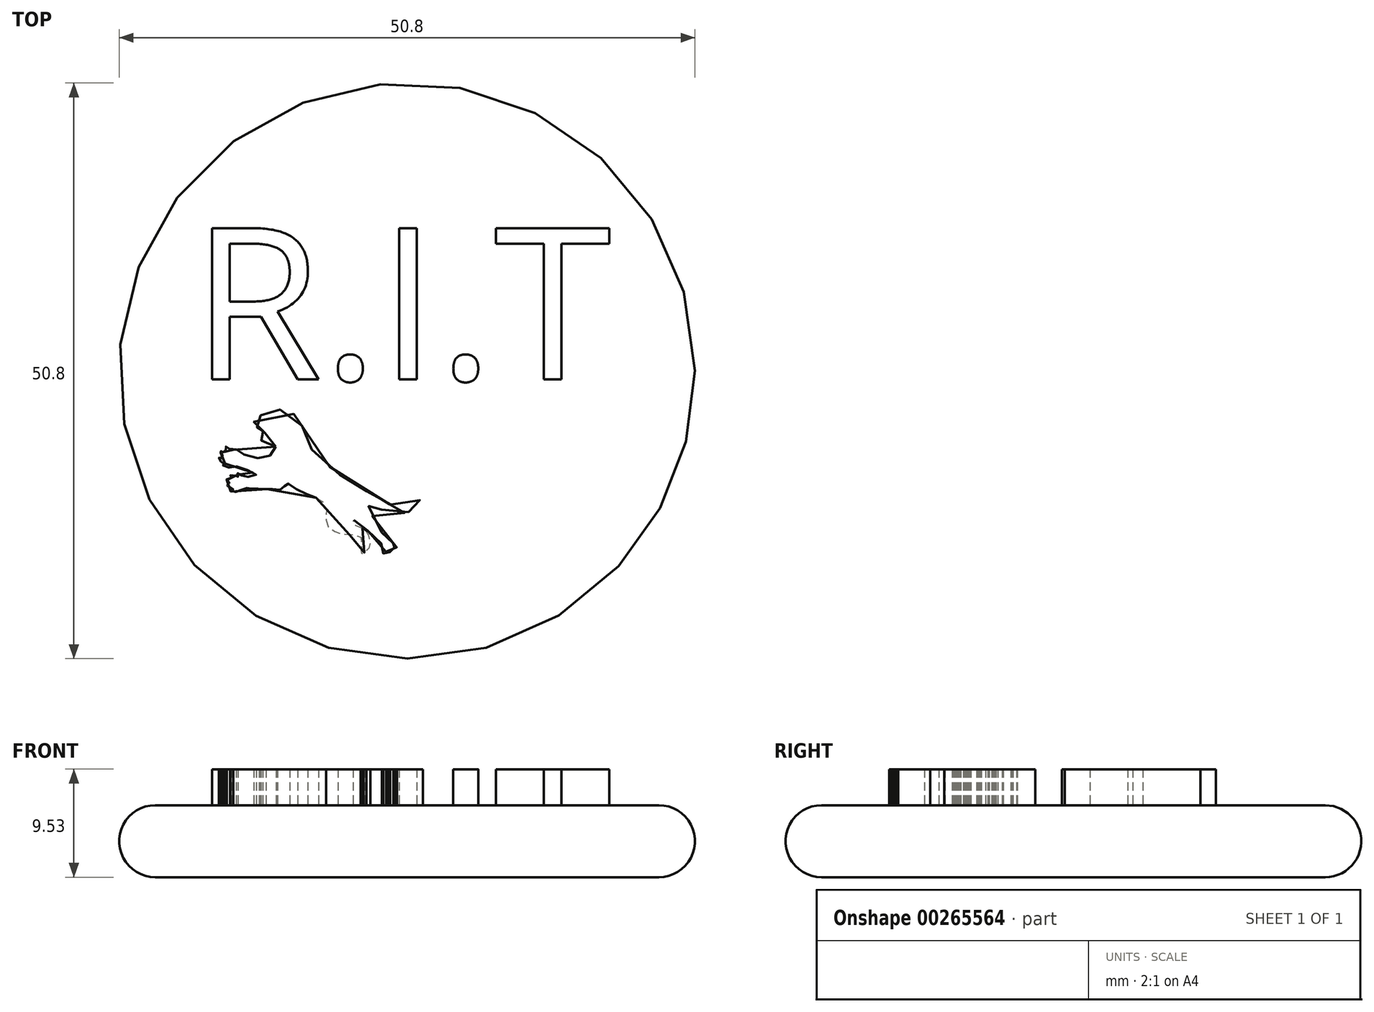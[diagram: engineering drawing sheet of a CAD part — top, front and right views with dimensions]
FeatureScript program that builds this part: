
annotation { "Feature Type Name" : "Feature", "Feature Type Description" : "" }
export const myFeature = defineFeature(function(context is Context, id is Id, definition is map)
    precondition{}
    {
        {
            var Q0;
            Q0=qCreatedBy(makeId("Top.planeOp"),FACE);
            var sketch = newSketch(context, id + "F0", { "sketchPlane" : qUnion([Q0])});
            skCircle(sketch, "E0", {"center": v(0, 0) * mm, "radius": 25.4 * mm});
            skText(sketch, "E1", { "text": "R.I.T\n", "fontName": "OpenSans-Regular.ttf"});
            skLineSegment(sketch, "E2", {"start": v(-19.05, 12.7) * mm, "end": v(19.05, -0.76) * mm});
            skPoint(sketch, "E3", {"position": v(0, 5.97) * mm});
            const initialGuessF0  = {"E1": [-0.01905, -0.00076, 1, 0, 0.01346]};
            skSetInitialGuess(sketch, initialGuessF0);
            skSolve(sketch);
        }
        {
            var Q0;
            Q0=makeQuery(id+"F0.imprint","IMPRINT",FACE,{"disambiguationData":[TD([[makeQuery(id+"F0.imprint","IMPRINT",EDGE,{"derivedFrom":sQuery(id+"F0.wireOp",EDGE,"E0")}),1.0]])]});
            var Q1;
            Q1=makeQuery(id+"F0.imprint","IMPRINT",FACE,{"disambiguationData":[TD([[makeQuery(id+"F0.imprint","IMPRINT",EDGE,{"derivedFrom":sQuery(id+"F0.wireOp",EDGE,"E1.sketch_text.stroke-11")}),1.0]])]});
            var Q2;
            {var subQ0=sQuery(id+"F0.wireOp",EDGE,"E1.sketch_text.stroke-15");Q2=makeQuery(id+"F0.imprint","IMPRINT",FACE,{"disambiguationData":[TD([[makeQuery(id+"F0.imprint","IMPRINT",EDGE,{"derivedFrom":subQ0}),1.0]])]});}
            extrude(context, id + "F1", {"entities" : qUnion([Q0, Q1, Q2]), "depth" : 6.35 * mm});
        }
        {
            var Q0;
            Q0=makeQuery(id+"F0.imprint","IMPRINT",FACE,{"disambiguationData":[TD([[makeQuery(id+"F0.imprint","IMPRINT",EDGE,{"derivedFrom":sQuery(id+"F0.wireOp",EDGE,"E1.sketch_text.stroke-18")}),-1.0]])]});
            var Q1;
            Q1=makeQuery(id+"F0.imprint","IMPRINT",FACE,{"disambiguationData":[TD([[makeQuery(id+"F0.imprint","IMPRINT",EDGE,{"derivedFrom":sQuery(id+"F0.wireOp",EDGE,"E1.sketch_text.stroke-30")}),-1.0]])]});
            var Q2;
            {var subQ0=sQuery(id+"F0.wireOp",EDGE,"E1.sketch_text.stroke-29");Q2=makeQuery(id+"F0.imprint","IMPRINT",FACE,{"disambiguationData":[TD([[makeQuery(id+"F0.imprint","IMPRINT",EDGE,{"derivedFrom":subQ0}),-1.0]])]});}
            var Q3;
            {var subQ0=sQuery(id+"F0.wireOp",EDGE,"E1.sketch_text.stroke-27");Q3=makeQuery(id+"F0.imprint","IMPRINT",FACE,{"disambiguationData":[TD([[makeQuery(id+"F0.imprint","IMPRINT",EDGE,{"derivedFrom":subQ0}),-1.0]])]});}
            var Q4;
            Q4=makeQuery(id+"F0.imprint","IMPRINT",FACE,{"disambiguationData":[TD([[makeQuery(id+"F0.imprint","IMPRINT",EDGE,{"derivedFrom":sQuery(id+"F0.wireOp",EDGE,"E1.sketch_text.stroke-0")}),-1.0]])]});
            var Q5;
            {var subQ7=sQuery(id+"F0.wireOp",EDGE,"E1.sketch_text.stroke-3");Q5=makeQuery(id+"F0.imprint","IMPRINT",FACE,{"disambiguationData":[TD([[makeQuery(id+"F0.imprint","IMPRINT",EDGE,{"derivedFrom":subQ7}),-1.0]])]});}
            var Q6;
            {var subQ0=sQuery(id+"F0.wireOp",EDGE,"E1.sketch_text.stroke-40");Q6=makeQuery(id+"F0.imprint","IMPRINT",FACE,{"disambiguationData":[TD([[makeQuery(id+"F0.imprint","IMPRINT",EDGE,{"derivedFrom":subQ0}),-1.0]])]});}
            var Q7;
            {var subQ0=sQuery(id+"F0.wireOp",EDGE,"E1.sketch_text.stroke-38");Q7=makeQuery(id+"F0.imprint","IMPRINT",FACE,{"disambiguationData":[TD([[makeQuery(id+"F0.imprint","IMPRINT",EDGE,{"derivedFrom":subQ0}),-1.0]])]});}
            extrude(context, id + "F2", {"entities" : qUnion([Q0, Q1, Q2, Q3, Q4, Q5, Q6, Q7]), "operationType" : NewBodyOperationType.ADD, "depth" : 9.52 * mm});
        }
        {
            var Q0;
            Q0=makeQuery(id+"F1.opExtrude","CAP_EDGE",EDGE,{"disambiguationData":[OSD([sQuery(id+"F0.wireOp",EDGE,"E0")])],"isStart":false});
            var Q1;
            Q1=makeQuery(id+"F1.opExtrude","CAP_EDGE",EDGE,{"disambiguationData":[OSD([sQuery(id+"F0.wireOp",EDGE,"E0")])],"isStart":true});
            fillet(context, id + "F3", {"entities" : qUnion([Q0, Q1]), "radius" : 3.17 * mm, "tangentPropagation" : true, "allowEdgeOverflow" : false});
        }
        {
            var Q0;
            Q0=makeQuery(id+"F1.opExtrude","CAP_FACE",FACE,{"disambiguationData":[OSD([sQuery(id+"F0.wireOp",EDGE,"E0"),sQuery(id+"F0.wireOp",EDGE,"E1.sketch_text.stroke-0"),sQuery(id+"F0.wireOp",EDGE,"E1.sketch_text.stroke-1"),sQuery(id+"F0.wireOp",EDGE,"E1.sketch_text.stroke-2"),sQuery(id+"F0.wireOp",EDGE,"E1.sketch_text.stroke-3"),sQuery(id+"F0.wireOp",EDGE,"E1.sketch_text.stroke-4"),sQuery(id+"F0.wireOp",EDGE,"E1.sketch_text.stroke-5"),sQuery(id+"F0.wireOp",EDGE,"E1.sketch_text.stroke-6"),sQuery(id+"F0.wireOp",EDGE,"E1.sketch_text.stroke-7"),sQuery(id+"F0.wireOp",EDGE,"E1.sketch_text.stroke-8"),sQuery(id+"F0.wireOp",EDGE,"E1.sketch_text.stroke-9"),sQuery(id+"F0.wireOp",EDGE,"E1.sketch_text.stroke-10"),sQuery(id+"F0.wireOp",EDGE,"E1.sketch_text.stroke-18"),sQuery(id+"F0.wireOp",EDGE,"E1.sketch_text.stroke-19"),sQuery(id+"F0.wireOp",EDGE,"E1.sketch_text.stroke-20"),sQuery(id+"F0.wireOp",EDGE,"E1.sketch_text.stroke-21"),sQuery(id+"F0.wireOp",EDGE,"E1.sketch_text.stroke-22"),sQuery(id+"F0.wireOp",EDGE,"E1.sketch_text.stroke-23"),sQuery(id+"F0.wireOp",EDGE,"E1.sketch_text.stroke-24"),sQuery(id+"F0.wireOp",EDGE,"E1.sketch_text.stroke-25"),sQuery(id+"F0.wireOp",EDGE,"E1.sketch_text.stroke-26"),sQuery(id+"F0.wireOp",EDGE,"E1.sketch_text.stroke-27"),sQuery(id+"F0.wireOp",EDGE,"E1.sketch_text.stroke-28"),sQuery(id+"F0.wireOp",EDGE,"E1.sketch_text.stroke-29"),sQuery(id+"F0.wireOp",EDGE,"E1.sketch_text.stroke-30"),sQuery(id+"F0.wireOp",EDGE,"E1.sketch_text.stroke-31"),sQuery(id+"F0.wireOp",EDGE,"E1.sketch_text.stroke-32"),sQuery(id+"F0.wireOp",EDGE,"E1.sketch_text.stroke-33"),sQuery(id+"F0.wireOp",EDGE,"E1.sketch_text.stroke-34"),sQuery(id+"F0.wireOp",EDGE,"E1.sketch_text.stroke-35"),sQuery(id+"F0.wireOp",EDGE,"E1.sketch_text.stroke-36"),sQuery(id+"F0.wireOp",EDGE,"E1.sketch_text.stroke-37"),sQuery(id+"F0.wireOp",EDGE,"E1.sketch_text.stroke-38"),sQuery(id+"F0.wireOp",EDGE,"E1.sketch_text.stroke-39"),sQuery(id+"F0.wireOp",EDGE,"E1.sketch_text.stroke-40"),sQuery(id+"F0.wireOp",EDGE,"E1.sketch_text.stroke-41"),sQuery(id+"F0.wireOp",EDGE,"E1.sketch_text.stroke-42"),sQuery(id+"F0.wireOp",EDGE,"E1.sketch_text.stroke-43"),sQuery(id+"F0.wireOp",EDGE,"E1.sketch_text.stroke-44"),sQuery(id+"F0.wireOp",EDGE,"E1.sketch_text.stroke-45")])],"isStart":false});
            var sketch = newSketch(context, id + "F4", { "sketchPlane" : qUnion([Q0])});
            skFitSpline(sketch, "E4", {"points": [v(-11.58, -6.67) * mm, v(-11.81, -7.02) * mm, v(-12.17, -7.55) * mm, v(-12.83, -7.73) * mm, v(-13.73, -7.57) * mm, v(-14.45, -7.34) * mm, v(-14.84, -7.04) * mm, v(-15.06, -6.93) * mm, v(-15.18, -7.06) * mm, v(-15.43, -6.95) * mm, v(-15.8, -6.87) * mm, v(-15.9, -6.83) * mm, v(-15.98, -6.83) * mm, v(-16.01, -6.75) * mm, v(-15.97, -6.67) * mm, v(-16.04, -6.7) * mm, v(-16.07, -6.81) * mm, v(-16.04, -6.96) * mm, v(-16.01, -7.01) * mm, v(-16.01, -7.13) * mm, v(-16.15, -7.1) * mm, v(-16.26, -7.13) * mm, v(-16.3, -7.2) * mm, v(-16.35, -7.16) * mm, v(-16.38, -7.07) * mm, v(-16.35, -7) * mm, v(-16.4, -7.03) * mm, v(-16.45, -7.12) * mm, v(-16.43, -7.28) * mm, v(-16.31, -7.42) * mm, v(-16.3, -7.4) * mm, v(-16.28, -7.48) * mm, v(-16.2, -7.55) * mm, v(-16.3, -7.55) * mm, v(-16.43, -7.65) * mm, v(-16.46, -7.73) * mm, v(-16.5, -7.7) * mm, v(-16.54, -7.66) * mm, v(-16.53, -7.53) * mm, v(-16.59, -7.58) * mm, v(-16.6, -7.71) * mm, v(-16.59, -7.83) * mm, v(-16.48, -7.9) * mm, v(-16.45, -8) * mm, v(-16.36, -8.07) * mm, v(-16.22, -8.14) * mm, v(-16.05, -8.14) * mm, v(-16.11, -8.2) * mm, v(-16.13, -8.35) * mm, v(-16.22, -8.32) * mm, v(-16.23, -8.22) * mm, v(-16.25, -8.3) * mm, v(-16.2, -8.45) * mm, v(-16, -8.52) * mm, v(-15.7, -8.54) * mm, v(-15.4, -8.44) * mm, v(-15.2, -8.4) * mm, v(-14.81, -8.5) * mm, v(-14.26, -8.7) * mm, v(-13.74, -8.92) * mm, v(-13.3, -9.16) * mm, v(-13.64, -9.2) * mm, v(-13.84, -9.26) * mm, v(-14.1, -9.4) * mm, v(-14.39, -9.4) * mm, v(-14.53, -9.3) * mm, v(-14.67, -9.2) * mm, v(-14.77, -9.2) * mm, v(-14.81, -9.09) * mm, v(-14.88, -9.04) * mm, v(-15, -9.04) * mm, v(-15.08, -9.08) * mm, v(-15.08, -9.15) * mm, v(-15.06, -9.11) * mm, v(-14.96, -9.1) * mm, v(-14.94, -9.21) * mm, v(-14.91, -9.3) * mm, v(-14.94, -9.34) * mm, v(-15.03, -9.28) * mm, v(-15.16, -9.25) * mm, v(-15.27, -9.25) * mm, v(-15.37, -9.27) * mm, v(-15.38, -9.27) * mm, v(-15.43, -9.22) * mm, v(-15.5, -9.2) * mm, v(-15.62, -9.23) * mm, v(-15.56, -9.24) * mm, v(-15.52, -9.25) * mm, v(-15.48, -9.35) * mm, v(-15.48, -9.44) * mm, v(-15.57, -9.44) * mm, v(-15.7, -9.56) * mm, v(-15.82, -9.53) * mm, v(-15.96, -9.62) * mm, v(-15.98, -9.7) * mm, v(-15.93, -9.66) * mm, v(-15.83, -9.64) * mm, v(-15.74, -9.73) * mm, v(-15.7, -9.85) * mm, v(-15.62, -9.94) * mm, v(-15.66, -10) * mm, v(-15.79, -9.98) * mm, v(-15.9, -10.15) * mm, v(-15.89, -10.22) * mm, v(-15.84, -10.15) * mm, v(-15.79, -10.1) * mm, v(-15.68, -10.15) * mm, v(-15.65, -10.24) * mm, v(-15.53, -10.35) * mm, v(-15.35, -10.47) * mm, v(-15.43, -10.49) * mm, v(-15.54, -10.5) * mm, v(-15.58, -10.61) * mm, v(-15.57, -10.69) * mm, v(-15.53, -10.6) * mm, v(-15.42, -10.58) * mm, v(-15.3, -10.6) * mm, v(-15.2, -10.67) * mm, v(-14.9, -10.64) * mm, v(-14.56, -10.48) * mm, v(-14.25, -10.36) * mm, v(-14, -10.34) * mm, v(-13.87, -10.4) * mm, v(-13.58, -10.37) * mm, v(-13.1, -10.42) * mm, v(-12.57, -10.45) * mm, v(-12.23, -10.44) * mm, v(-11.6, -10.46) * mm, v(-11.14, -10.48) * mm, v(-10.91, -10.29) * mm, v(-10.76, -10.04) * mm, v(-10.56, -9.93) * mm, v(-10, -10.3) * mm, v(-8.9, -10.85) * mm, v(-8.04, -11.18) * mm, v(-7.4, -11.59) * mm, v(-7.16, -12.08) * mm, v(-7.11, -13) * mm, v(-7.14, -13.45) * mm, v(-6.76, -13.95) * mm, v(-6.26, -14.23) * mm, v(-5.75, -14.4) * mm, v(-4.63, -14.48) * mm, v(-4.14, -14.6) * mm, v(-4, -15.08) * mm, v(-4.06, -15.45) * mm, v(-4.1, -15.68) * mm, v(-4.06, -15.85) * mm, v(-4.08, -15.96) * mm, v(-4.06, -16.07) * mm, v(-3.94, -16.14) * mm, v(-3.83, -16.17) * mm, v(-3.88, -16.13) * mm, v(-3.95, -16.07) * mm, v(-3.98, -16) * mm, v(-3.9, -16.02) * mm, v(-3.68, -16.02) * mm, v(-3.58, -15.94) * mm, v(-3.57, -15.83) * mm, v(-3.46, -15.74) * mm, v(-3.33, -15.61) * mm, v(-3.26, -15.46) * mm, v(-3.25, -15.28) * mm, v(-3.26, -15.04) * mm, v(-3.29, -14.95) * mm, v(-3.33, -14.77) * mm, v(-3.35, -14.6) * mm, v(-3.4, -14.44) * mm, v(-3.49, -14.2) * mm, v(-3.7, -14) * mm, v(-3.93, -13.9) * mm, v(-4.13, -13.82) * mm, v(-4.42, -13.7) * mm, v(-4.62, -13.6) * mm, v(-4.73, -13.48) * mm, v(-4.76, -13.35) * mm, v(-4.74, -13.2) * mm, v(-4.72, -13.13) * mm, v(-4.62, -13.24) * mm, v(-4.4, -13.46) * mm, v(-4.24, -13.58) * mm, v(-3.93, -13.75) * mm, v(-3.66, -13.97) * mm, v(-3.46, -14.12) * mm, v(-3.24, -14.36) * mm, v(-2.99, -14.56) * mm, v(-2.77, -14.73) * mm, v(-2.51, -14.94) * mm, v(-2.18, -15.47) * mm, v(-2.2, -15.77) * mm, v(-2.2, -15.95) * mm, v(-2.17, -16) * mm, v(-2.17, -16.18) * mm, v(-2.08, -16.26) * mm, v(-2.11, -16.19) * mm, v(-2.07, -16.05) * mm, v(-2, -16.04) * mm, v(-1.85, -15.95) * mm, v(-1.85, -16.03) * mm, v(-1.7, -16.17) * mm, v(-1.73, -16.08) * mm, v(-1.73, -15.99) * mm, v(-1.6, -16.01) * mm, v(-1.5, -15.92) * mm, v(-1.52, -15.81) * mm, v(-1.38, -15.86) * mm, v(-1.25, -15.84) * mm, v(-1.2, -15.9) * mm, v(-1.2, -15.78) * mm, v(-1.16, -15.66) * mm, v(-1.2, -15.58) * mm, v(-1.08, -15.55) * mm, v(-0.97, -15.46) * mm, v(-0.96, -15.57) * mm, v(-0.97, -15.65) * mm, v(-0.9, -15.55) * mm, v(-0.9, -15.38) * mm, v(-1, -15.25) * mm, v(-1.08, -15.2) * mm, v(-1.46, -15.13) * mm, v(-1.49, -14.97) * mm, v(-1.59, -14.73) * mm, v(-1.69, -14.63) * mm, v(-1.9, -14.54) * mm, v(-2.25, -14.24) * mm, v(-2.56, -13.85) * mm, v(-3.02, -13) * mm, v(-3.33, -12.06) * mm, v(-3.68, -11.36) * mm, v(-3.28, -11.49) * mm, v(-2.62, -11.96) * mm, v(-1.89, -12.47) * mm, v(-1.08, -12.62) * mm, v(-0.4, -12.55) * mm, v(0.34, -12.4) * mm, v(1.2, -12.03) * mm, v(1.39, -11.78) * mm, v(1.33, -11.57) * mm, v(1.16, -11.41) * mm, v(0.73, -11.54) * mm, v(-0.31, -11.84) * mm, v(-1.24, -11.84) * mm, v(-2.01, -11.6) * mm, v(-2.67, -11.1) * mm, v(-3.23, -10.72) * mm, v(-3.86, -10.57) * mm, v(-4.17, -10.49) * mm, v(-4.79, -10.09) * mm, v(-6.73, -8.55) * mm, v(-7.96, -7.53) * mm, v(-8.36, -7) * mm, v(-8.51, -6.62) * mm, v(-8.6, -6.22) * mm, v(-8.92, -5.7) * mm, v(-9.37, -4.6) * mm, v(-10.06, -3.76) * mm, v(-10.65, -3.39) * mm, v(-11.3, -3.41) * mm, v(-11.7, -3.4) * mm, v(-12.34, -3.57) * mm, v(-12.77, -3.73) * mm, v(-12.87, -3.9) * mm, v(-13.18, -4.04) * mm, v(-13.32, -4.22) * mm, v(-13.5, -4.34) * mm, v(-13.48, -4.6) * mm, v(-13.28, -4.85) * mm, v(-13.25, -4.96) * mm, v(-13.2, -4.95) * mm, v(-12.98, -5.33) * mm, v(-12.96, -5.24) * mm, v(-12.97, -5.03) * mm, v(-12.87, -5.22) * mm, v(-12.77, -5.36) * mm, v(-12.73, -5.18) * mm, v(-12.73, -4.97) * mm, v(-12.67, -4.96) * mm, v(-12.5, -5.1) * mm, v(-12.45, -5.27) * mm, v(-12.51, -5.45) * mm, v(-12.69, -5.5) * mm, v(-12.77, -5.42) * mm, v(-12.8, -5.48) * mm, v(-12.99, -5.37) * mm, v(-12.94, -5.56) * mm, v(-13.04, -5.64) * mm, v(-13.01, -5.95) * mm, v(-12.92, -6.1) * mm, v(-12.64, -6.25) * mm, v(-12.15, -6.26) * mm, v(-11.81, -6.2) * mm, v(-11.58, -6.32) * mm, v(-11.58, -6.67) * mm]});
            skSolve(sketch);
        }
        {
            var Q0;
            Q0 = qSketchRegion(id + "F4", true);
            extrude(context, id + "F5", {"entities" : qUnion([Q0]), "operationType" : NewBodyOperationType.ADD, "depth" : 3.17 * mm});
        }
    });
